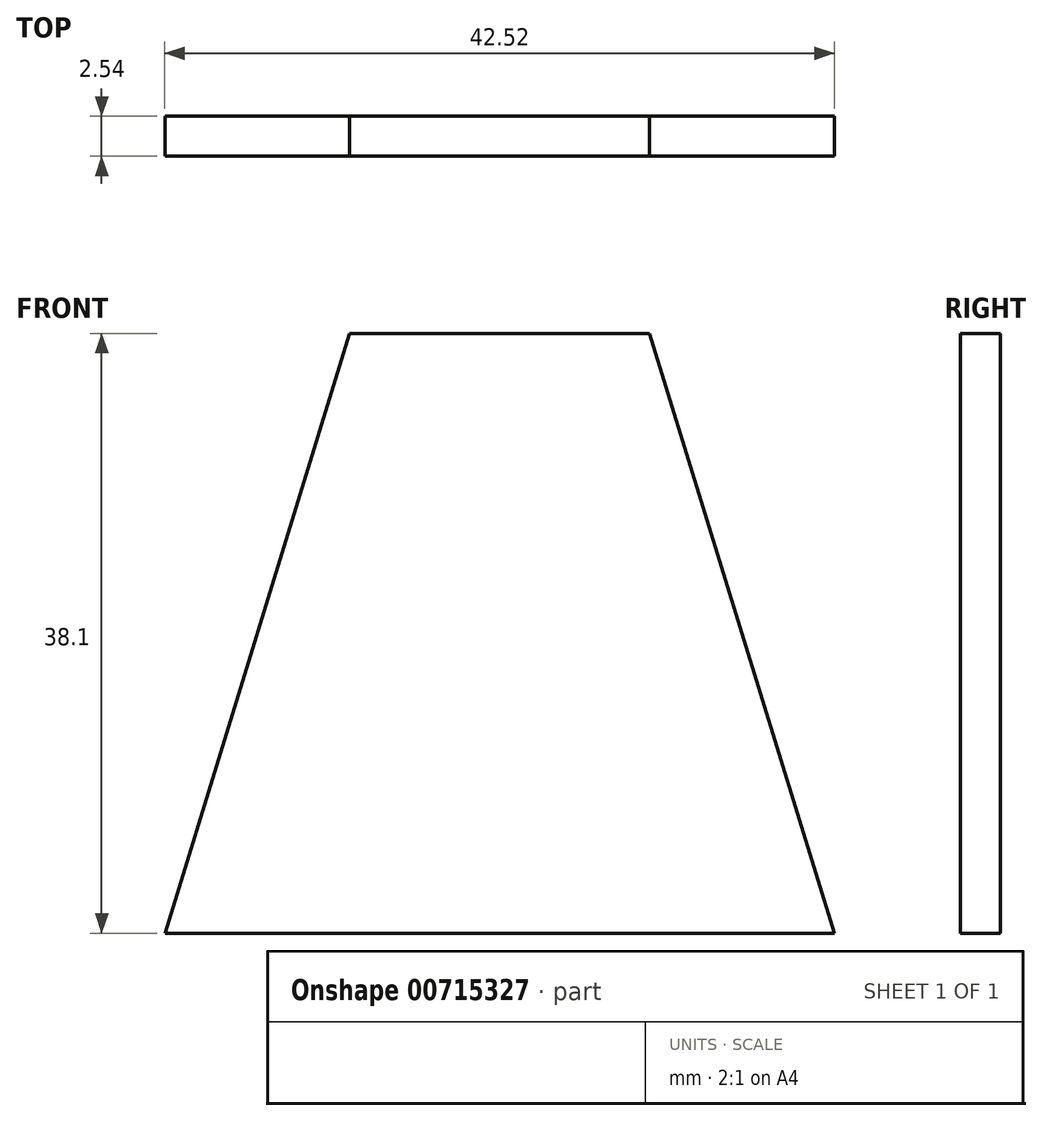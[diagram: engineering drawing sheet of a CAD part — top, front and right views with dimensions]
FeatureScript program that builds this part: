
annotation { "Feature Type Name" : "Feature", "Feature Type Description" : "" }
export const myFeature = defineFeature(function(context is Context, id is Id, definition is map)
    precondition{}
    {
        {
            var Q0;
            Q0=qCreatedBy(makeId("Front.planeOp"),FACE);
            var sketch = newSketch(context, id + "F0", { "sketchPlane" : qUnion([Q0])});
            skLineSegment(sketch, "E0", {"start": v(0, 0) * mm, "end": v(0, 38.1) * mm});
            skLineSegment(sketch, "E1", {"start": v(0, 38.1) * mm, "end": v(-9.53, 38.1) * mm});
            skLineSegment(sketch, "E2", {"start": v(-9.53, 38.1) * mm, "end": v(-21.26, 0) * mm});
            skLineSegment(sketch, "E3", {"start": v(0, 38.1) * mm, "end": v(9.52, 38.1) * mm});
            skLineSegment(sketch, "E4", {"start": v(-21.26, 0) * mm, "end": v(0, 0) * mm});
            skLineSegment(sketch, "E5", {"start": v(0, 0) * mm, "end": v(21.26, 0) * mm});
            skLineSegment(sketch, "E6", {"start": v(21.26, 0) * mm, "end": v(9.52, 38.1) * mm});
            skSolve(sketch);
        }
        {
            var Q0;
            Q0=qSketchRegion(id+"F0",true);
            extrude(context, id + "F1", {"entities" : qUnion([Q0]), "depth" : 2.54 * mm, "offsetDistance" : 25.4 * mm});
        }
    });
